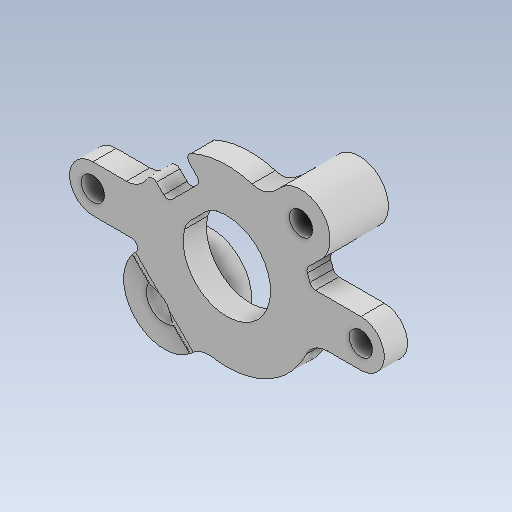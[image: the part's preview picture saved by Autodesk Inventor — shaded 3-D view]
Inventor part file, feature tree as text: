
AUTODESK INVENTOR PART (.ipt)
format: ipt  version: 2020 (Build 240168000, 168)  size: 306,176 bytes
history: native  units: mm
features: sketch x5, other x3
ambient origin geometry x8: Origin, YZ Plane, XZ Plane, XY Plane, X Axis, Y Axis, Z Axis, Center Point
bodies: Solid1 (feature_tree)
feature tree (8):
  other  "encoder_holder_2.ipt"
  other  "Solid1::encoder_holder_2.ipt"
  other  "TaggingFeature1"
  sketch  "Sketch1"  dims[d0=10.0mm]
  sketch  "Sketch2"
  sketch  "Sketch3"
  sketch  "Sketch4"
  sketch  "Sketch5"
